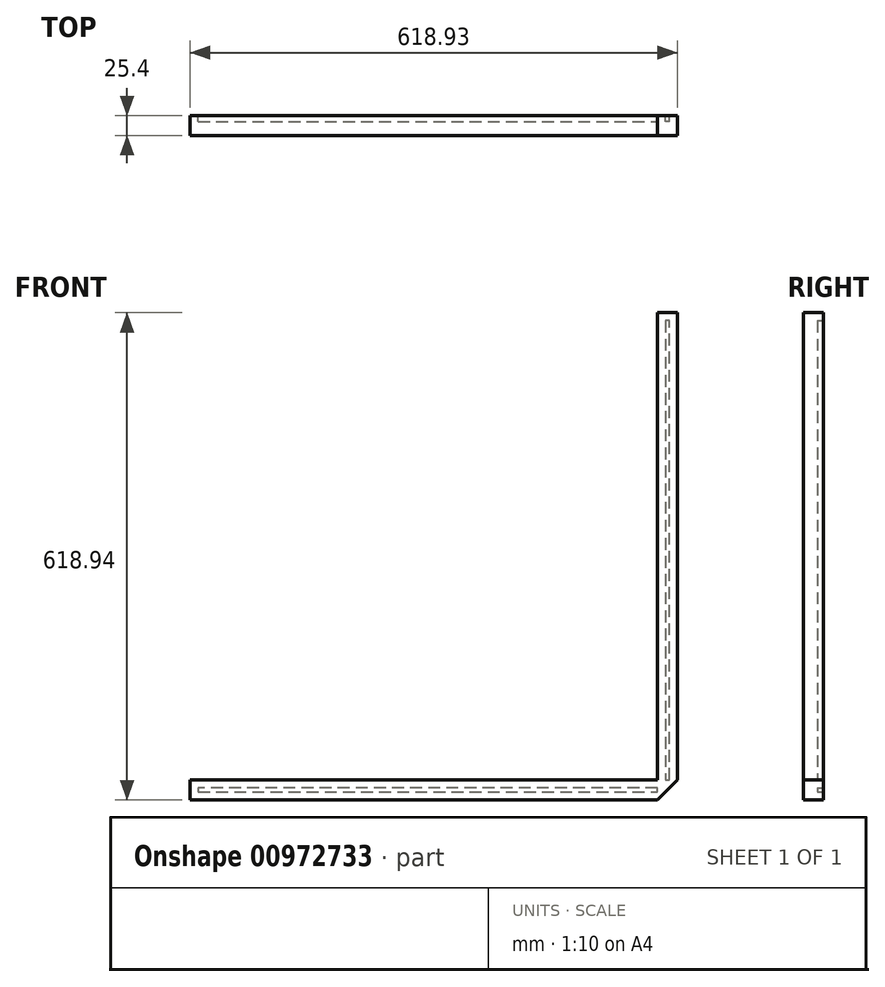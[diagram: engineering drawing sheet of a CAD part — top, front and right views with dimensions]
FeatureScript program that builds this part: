
annotation { "Feature Type Name" : "Feature", "Feature Type Description" : "" }
export const myFeature = defineFeature(function(context is Context, id is Id, definition is map)
    precondition{}
    {
        {
            var Q0;
            Q0=qCreatedBy(makeId("Front.planeOp"),FACE);
            var sketch = newSketch(context, id + "F0", { "sketchPlane" : qUnion([Q0])});
            skLineSegment(sketch, "E0", {"start": v(-505.21, -131.65) * mm, "end": v(-505.21, -106.25) * mm});
            skLineSegment(sketch, "E1", {"start": v(-505.21, -106.25) * mm, "end": v(88.32, -106.25) * mm});
            skLineSegment(sketch, "E2", {"start": v(88.32, -106.25) * mm, "end": v(88.32, -131.65) * mm});
            skLineSegment(sketch, "E3", {"start": v(88.32, -131.65) * mm, "end": v(-505.21, -131.65) * mm});
            skLineSegment(sketch, "E4", {"start": v(88.32, -106.25) * mm, "end": v(113.72, -106.25) * mm});
            skLineSegment(sketch, "E5", {"start": v(113.72, -106.25) * mm, "end": v(113.72, 487.3) * mm});
            skLineSegment(sketch, "E6", {"start": v(113.72, 487.3) * mm, "end": v(88.32, 487.3) * mm});
            skLineSegment(sketch, "E7", {"start": v(88.32, 487.3) * mm, "end": v(88.32, -106.25) * mm});
            skLineSegment(sketch, "E8", {"start": v(113.72, -106.25) * mm, "end": v(88.32, -131.65) * mm});
            skSolve(sketch);
        }
        {
            var Q0;
            Q0=makeQuery(id+"F0.imprint","IMPRINT",FACE,{"disambiguationData":[TD([[makeQuery(id+"F0.imprint","IMPRINT",EDGE,{"derivedFrom":sQuery(id+"F0.wireOp",EDGE,"E4")}),1.0]])]});
            var Q1;
            Q1=makeQuery(id+"F0.imprint","IMPRINT",FACE,{"disambiguationData":[TD([[makeQuery(id+"F0.imprint","IMPRINT",EDGE,{"derivedFrom":sQuery(id+"F0.wireOp",EDGE,"E2")}),1.0]])]});
            var Q2;
            Q2=makeQuery(id+"F0.imprint","IMPRINT",FACE,{"disambiguationData":[TD([[makeQuery(id+"F0.imprint","IMPRINT",EDGE,{"derivedFrom":sQuery(id+"F0.wireOp",EDGE,"E0")}),-1.0]])]});
            extrude(context, id + "F1", {"entities" : qUnion([Q0, Q1, Q2]), "depth" : 25.4 * mm, "offsetDistance" : 25.4 * mm});
        }
        {
            var Q0;
            Q0=makeQuery(id+"F1.opExtrude","CAP_FACE",FACE,{"disambiguationData":[OSD([sQuery(id+"F0.wireOp",EDGE,"E0"),sQuery(id+"F0.wireOp",EDGE,"E1"),sQuery(id+"F0.wireOp",EDGE,"E3"),sQuery(id+"F0.wireOp",EDGE,"E5"),sQuery(id+"F0.wireOp",EDGE,"E6"),sQuery(id+"F0.wireOp",EDGE,"E7"),sQuery(id+"F0.wireOp",EDGE,"E8")])],"isStart":true});
            var sketch = newSketch(context, id + "F2", { "sketchPlane" : qUnion([Q0])});
            skLineSegment(sketch, "E9", {"start": v(-113.72, 487.3) * mm, "end": v(-103.56, 487.3) * mm});
            skLineSegment(sketch, "E10", {"start": v(-88.32, 487.3) * mm, "end": v(-98.48, 487.3) * mm});
            skLineSegment(sketch, "E11", {"start": v(-98.48, 487.3) * mm, "end": v(-98.48, -106.25) * mm});
            skLineSegment(sketch, "E12", {"start": v(-98.48, -106.25) * mm, "end": v(-103.56, -106.25) * mm});
            skLineSegment(sketch, "E13", {"start": v(-103.56, -106.25) * mm, "end": v(-103.56, 487.3) * mm});
            skLineSegment(sketch, "E14", {"start": v(-103.56, 487.3) * mm, "end": v(-103.56, 477.13) * mm});
            skLineSegment(sketch, "E15", {"start": v(-103.56, 477.13) * mm, "end": v(-98.48, 477.13) * mm});
            skSolve(sketch);
        }
        {
            var Q0;
            {var subQ0=sQuery(id+"F2.wireOp",EDGE,"E12");Q0=makeQuery(id+"F2.imprint","IMPRINT",FACE,{"disambiguationData":[TD([[makeQuery(id+"F2.imprint","IMPRINT",EDGE,{"derivedFrom":subQ0}),-1.0]])]});}
            extrude(context, id + "F3", {"entities" : qUnion([Q0]), "operationType" : NewBodyOperationType.REMOVE, "oppositeDirection" : true, "depth" : 7.62 * mm, "offsetDistance" : 25.4 * mm});
        }
        {
            var Q0;
            Q0=makeQuery(id+"F1.opExtrude","CAP_FACE",FACE,{"disambiguationData":[OSD([sQuery(id+"F0.wireOp",EDGE,"E0"),sQuery(id+"F0.wireOp",EDGE,"E1"),sQuery(id+"F0.wireOp",EDGE,"E3"),sQuery(id+"F0.wireOp",EDGE,"E5"),sQuery(id+"F0.wireOp",EDGE,"E6"),sQuery(id+"F0.wireOp",EDGE,"E7"),sQuery(id+"F0.wireOp",EDGE,"E8")])],"isStart":true});
            var sketch = newSketch(context, id + "F4", { "sketchPlane" : qUnion([Q0])});
            skLineSegment(sketch, "E16", {"start": v(505.21, -106.25) * mm, "end": v(505.21, -116.41) * mm});
            skLineSegment(sketch, "E17", {"start": v(505.21, -131.65) * mm, "end": v(505.21, -121.5) * mm});
            skLineSegment(sketch, "E18", {"start": v(505.21, -121.5) * mm, "end": v(-88.32, -121.5) * mm});
            skLineSegment(sketch, "E19", {"start": v(-88.32, -121.5) * mm, "end": v(-88.32, -116.41) * mm});
            skLineSegment(sketch, "E20", {"start": v(-88.32, -116.41) * mm, "end": v(505.21, -116.41) * mm});
            skLineSegment(sketch, "E21", {"start": v(505.21, -116.41) * mm, "end": v(495.05, -116.41) * mm});
            skLineSegment(sketch, "E22", {"start": v(495.05, -116.41) * mm, "end": v(495.05, -121.5) * mm});
            skSolve(sketch);
        }
        {
            var Q0;
            {var subQ0=sQuery(id+"F4.wireOp",EDGE,"E19");Q0=makeQuery(id+"F4.imprint","IMPRINT",FACE,{"disambiguationData":[TD([[makeQuery(id+"F4.imprint","IMPRINT",EDGE,{"derivedFrom":subQ0}),-1.0]])]});}
            extrude(context, id + "F5", {"entities" : qUnion([Q0]), "operationType" : NewBodyOperationType.REMOVE, "oppositeDirection" : true, "depth" : 7.62 * mm, "offsetDistance" : 25.4 * mm});
        }
    });
